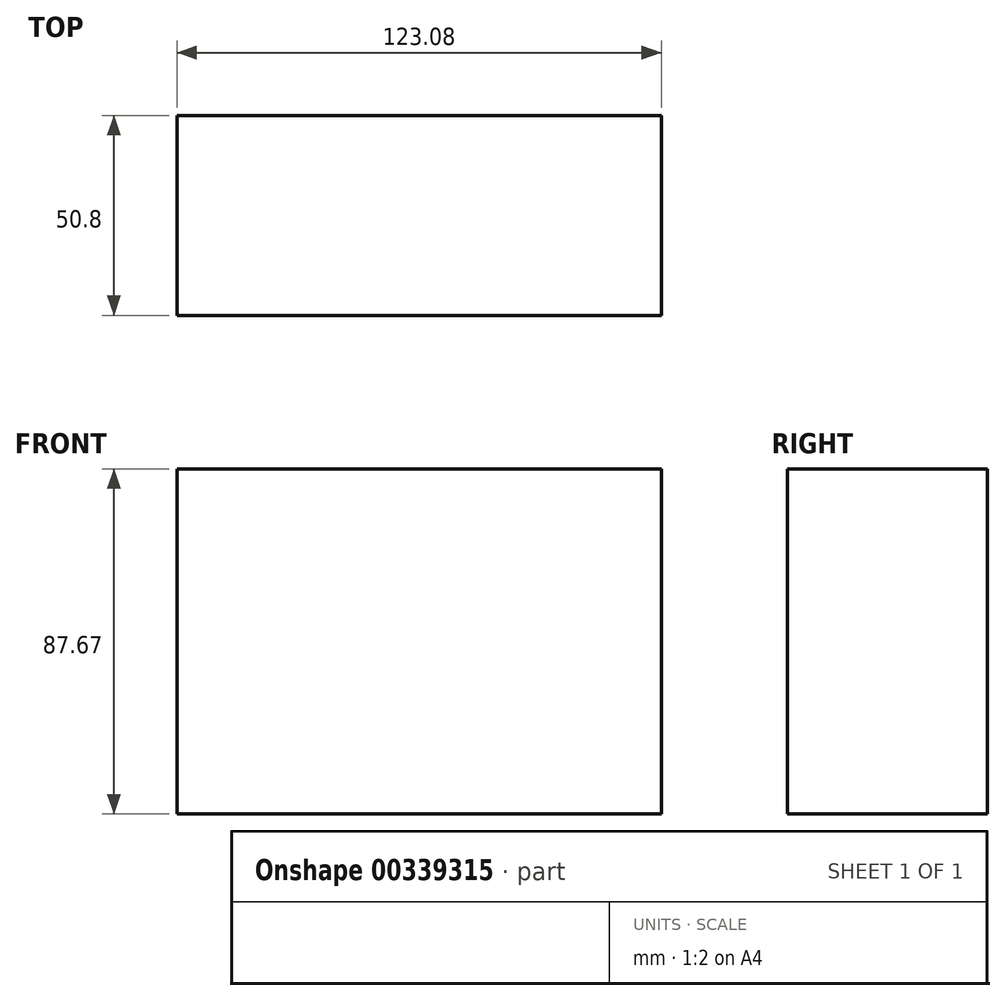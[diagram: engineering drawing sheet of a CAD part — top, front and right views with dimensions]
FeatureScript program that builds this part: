
annotation { "Feature Type Name" : "Feature", "Feature Type Description" : "" }
export const myFeature = defineFeature(function(context is Context, id is Id, definition is map)
    precondition{}
    {
        {
            var Q0;
            Q0=qCreatedBy(makeId("Front.planeOp"),FACE);
            var sketch = newSketch(context, id + "F0", { "sketchPlane" : qUnion([Q0])});
            skLineSegment(sketch, "E0.bottom", {"start": v(-55.64, 43.07) * mm, "end": v(67.44, 43.07) * mm});
            skLineSegment(sketch, "E0.top", {"start": v(-55.64, -44.6) * mm, "end": v(67.44, -44.6) * mm});
            skLineSegment(sketch, "E0.left", {"start": v(-55.64, 43.07) * mm, "end": v(-55.64, -44.6) * mm});
            skLineSegment(sketch, "E0.right", {"start": v(67.44, 43.07) * mm, "end": v(67.44, -44.6) * mm});
            skSolve(sketch);
        }
        {
            var Q0;
            Q0 = qSketchRegion(id + "F0", true);
            extrude(context, id + "F1", {"entities" : qUnion([Q0]), "depth" : 50.8 * mm});
        }
    });
